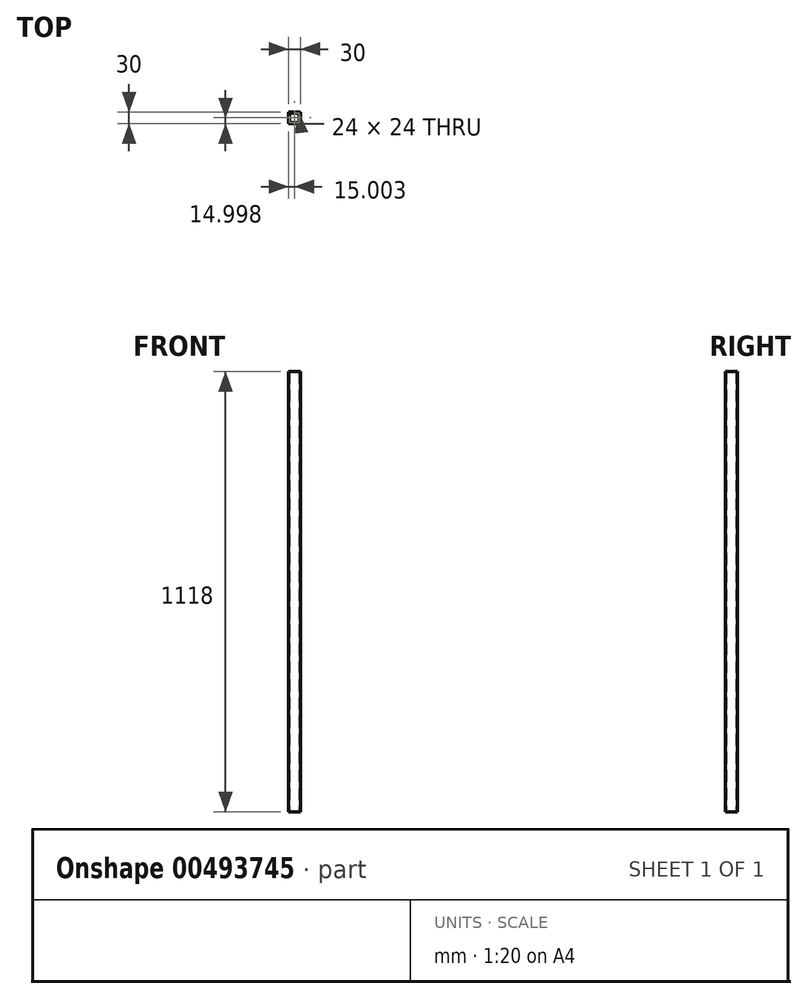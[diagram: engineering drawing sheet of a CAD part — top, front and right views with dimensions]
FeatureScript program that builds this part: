
annotation { "Feature Type Name" : "Feature", "Feature Type Description" : "" }
export const myFeature = defineFeature(function(context is Context, id is Id, definition is map)
    precondition{}
    {
        {
            var Q0;
            Q0=qCreatedBy(makeId("Top.planeOp"),FACE);
            var sketch = newSketch(context, id + "F0", { "sketchPlane" : qUnion([Q0])});
            skLineSegment(sketch, "E0.bottom", {"start": v(-15.76, 12.18) * mm, "end": v(8.24, 12.18) * mm});
            skLineSegment(sketch, "E0.top", {"start": v(-15.76, -11.82) * mm, "end": v(8.24, -11.82) * mm});
            skLineSegment(sketch, "E0.left", {"start": v(-15.76, 12.18) * mm, "end": v(-15.76, -11.82) * mm});
            skLineSegment(sketch, "E0.right", {"start": v(8.24, 12.18) * mm, "end": v(8.24, -11.82) * mm});
            skLineSegment(sketch, "E1.bottom", {"start": v(-18.76, 15.18) * mm, "end": v(11.24, 15.18) * mm});
            skLineSegment(sketch, "E1.top", {"start": v(-18.76, -14.82) * mm, "end": v(11.24, -14.82) * mm});
            skLineSegment(sketch, "E1.left", {"start": v(-18.76, 15.18) * mm, "end": v(-18.76, -14.82) * mm});
            skLineSegment(sketch, "E1.right", {"start": v(11.24, 15.18) * mm, "end": v(11.24, -14.82) * mm});
            skSolve(sketch);
        }
        {
            var Q0;
            Q0 = qSketchRegion(id + "F0", true);
            extrude(context, id + "F1", {"entities" : qUnion([Q0]), "flatOperationType" : FlatOperationType.REMOVE, "offsetDistance" : 25 * mm, "depth" : 1118 * mm, "domain" : OperationDomain.MODEL});
        }
    });
